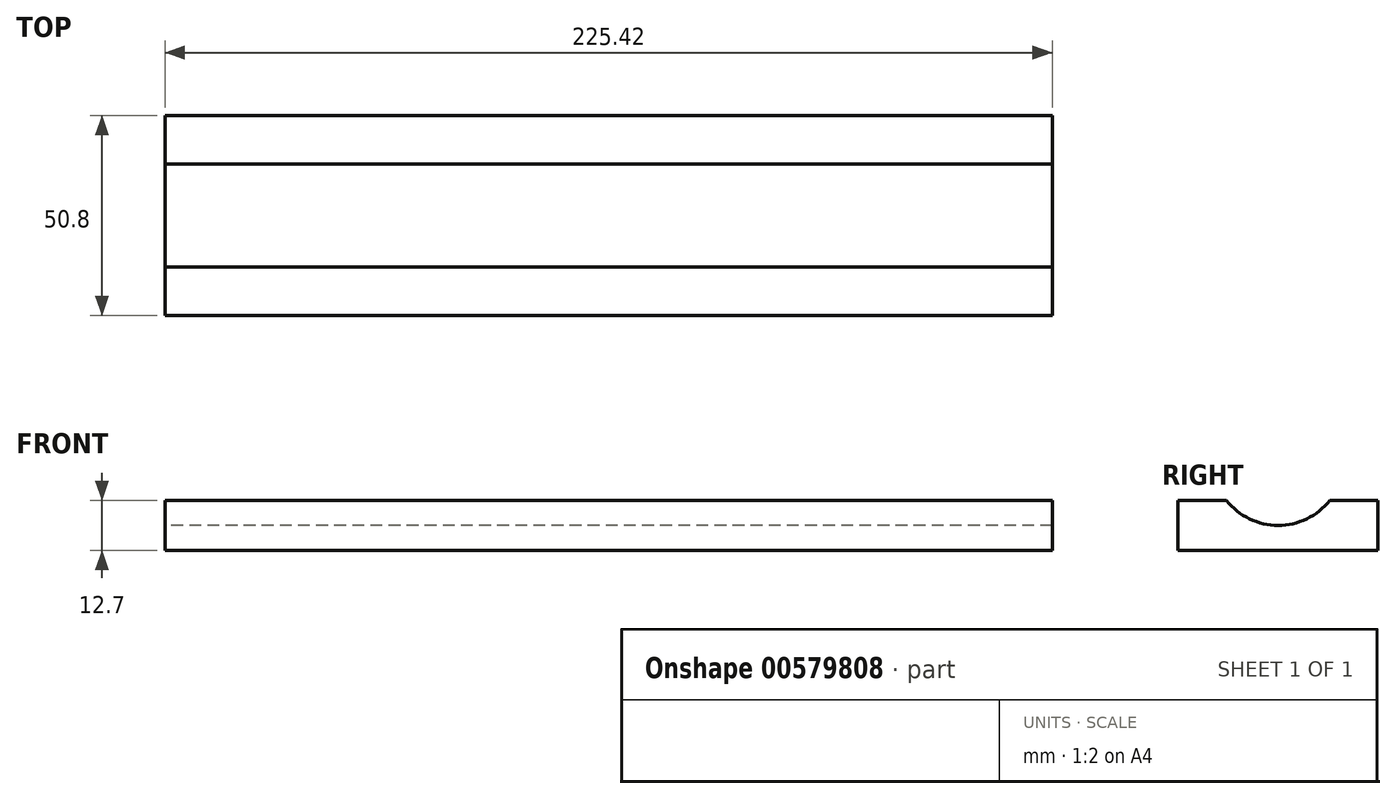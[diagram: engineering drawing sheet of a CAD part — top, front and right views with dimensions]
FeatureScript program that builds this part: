
annotation { "Feature Type Name" : "Feature", "Feature Type Description" : "" }
export const myFeature = defineFeature(function(context is Context, id is Id, definition is map)
    precondition{}
    {
        {
            var Q0;
            Q0=qCreatedBy(makeId("Right.planeOp"),FACE);
            var sketch = newSketch(context, id + "F0", { "sketchPlane" : qUnion([Q0])});
            skLineSegment(sketch, "E0.bottom", {"start": v(-25.4, 6.35) * mm, "end": v(25.4, 6.35) * mm});
            skLineSegment(sketch, "E0.top", {"start": v(-25.4, -6.35) * mm, "end": v(25.4, -6.35) * mm});
            skLineSegment(sketch, "E0.left", {"start": v(-25.4, 6.35) * mm, "end": v(-25.4, -6.35) * mm});
            skLineSegment(sketch, "E0.right", {"start": v(25.4, 6.35) * mm, "end": v(25.4, -6.35) * mm});
            skPoint(sketch, "E0.middle", {"position": v(0, 0) * mm});
            skSolve(sketch);
        }
        {
            var Q0;
            Q0=qSketchRegion(id+"F0",true);
            extrude(context, id + "F1", {"entities" : qUnion([Q0]), "depth" : 225.42 * mm, "offsetDistance" : 25.4 * mm});
        }
        {
            var Q0;
            Q0=makeQuery(id+"F1.opExtrude","CAP_FACE",FACE,{"disambiguationData":[OSD([sQuery(id+"F0.wireOp",EDGE,"E0.bottom"),sQuery(id+"F0.wireOp",EDGE,"E0.top"),sQuery(id+"F0.wireOp",EDGE,"E0.left"),sQuery(id+"F0.wireOp",EDGE,"E0.right")])],"isStart":true});
            var sketch = newSketch(context, id + "F2", { "sketchPlane" : qUnion([Q0])});
            skCircle(sketch, "E1", {"center": v(0, 16.65) * mm, "radius": 16.65 * mm});
            skSolve(sketch);
        }
        {
            var Q0;
            Q0=qSketchRegion(id+"F2",true);
            extrude(context, id + "F3", {"entities" : qUnion([Q0]), "operationType" : NewBodyOperationType.REMOVE, "oppositeDirection" : true, "depth" : 266.7 * mm, "offsetDistance" : 25.4 * mm});
        }
    });
